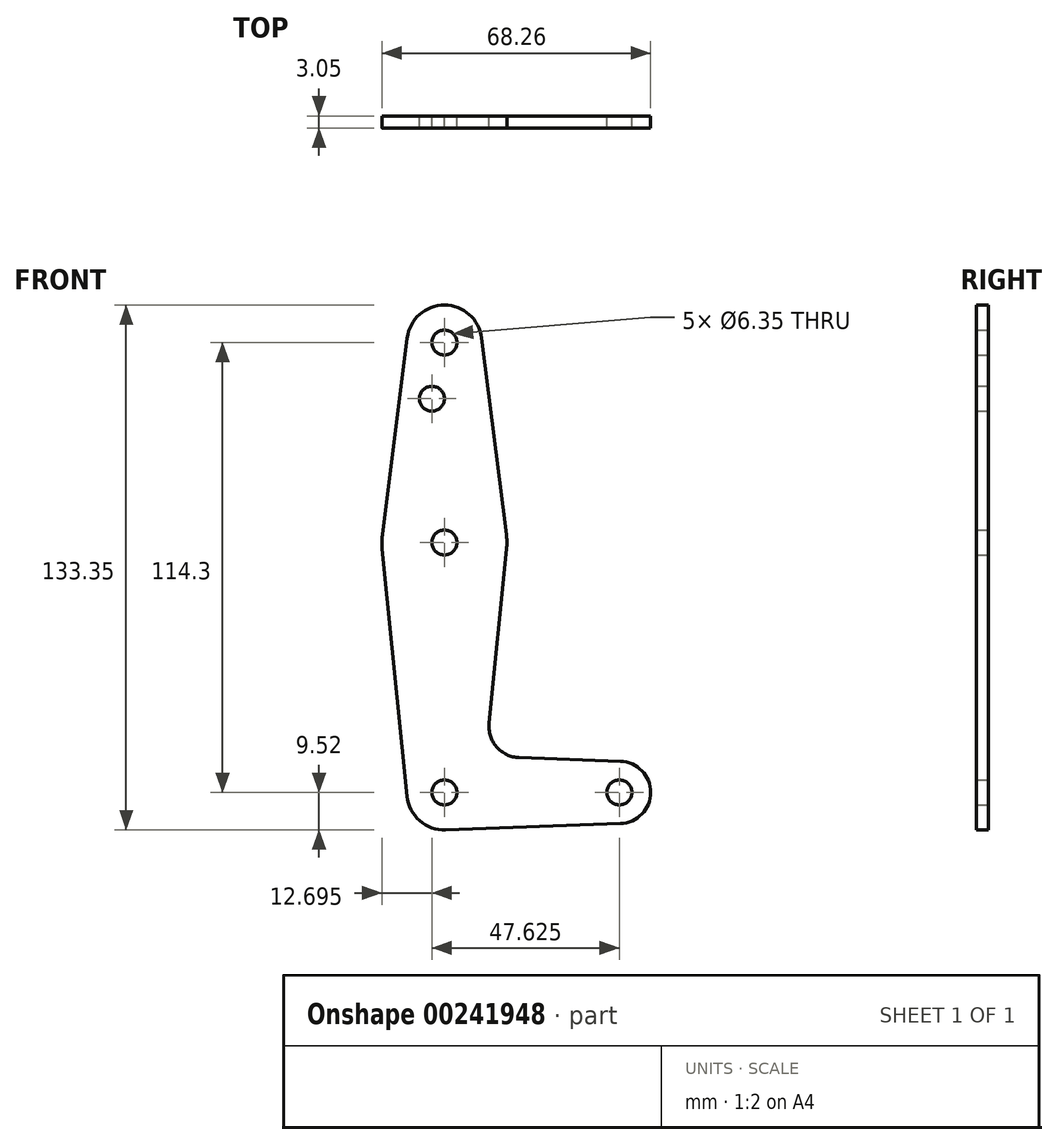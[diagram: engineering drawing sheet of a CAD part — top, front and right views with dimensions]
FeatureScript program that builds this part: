
annotation { "Feature Type Name" : "Feature", "Feature Type Description" : "" }
export const myFeature = defineFeature(function(context is Context, id is Id, definition is map)
    precondition{}
    {
        {
            var Q0;
            Q0=qCreatedBy(makeId("Front.planeOp"),FACE);
            var sketch = newSketch(context, id + "F0", { "sketchPlane" : qUnion([Q0])});
            skLineSegment(sketch, "E0", {"start": v(0, 0) * mm, "end": v(0, 114.3) * mm, "construction": true});
            skLineSegment(sketch, "E1", {"start": v(0, 0) * mm, "end": v(44.45, 0) * mm, "construction": true});
            skCircle(sketch, "E2", {"center": v(0, 114.3) * mm, "radius": 9.53 * mm});
            skCircle(sketch, "E3", {"center": v(0, 63.5) * mm, "radius": 15.88 * mm});
            skCircle(sketch, "E4", {"center": v(0, 0) * mm, "radius": 9.53 * mm});
            skCircle(sketch, "E5", {"center": v(44.45, 0) * mm, "radius": 7.94 * mm});
            skLineSegment(sketch, "E6", {"start": v(-9.45, 115.5) * mm, "end": v(-15.75, 65.48) * mm});
            skLineSegment(sketch, "E7", {"start": v(-9.48, -0.95) * mm, "end": v(-15.8, 61.91) * mm});
            skLineSegment(sketch, "E8", {"start": v(11.34, 17.6) * mm, "end": v(15.8, 61.91) * mm});
            skLineSegment(sketch, "E9", {"start": v(9.45, 115.5) * mm, "end": v(15.75, 65.48) * mm});
            skLineSegment(sketch, "E10", {"start": v(18.97, 8.85) * mm, "end": v(44.73, 7.93) * mm});
            skLineSegment(sketch, "E11", {"start": v(44.73, -7.93) * mm, "end": v(0, -9.53) * mm});
            skCircle(sketch, "E12", {"center": v(0, 114.3) * mm, "radius": 3.18 * mm});
            skCircle(sketch, "E13", {"center": v(0, 63.5) * mm, "radius": 3.18 * mm});
            skCircle(sketch, "E14", {"center": v(0, 0) * mm, "radius": 3.18 * mm});
            skCircle(sketch, "E15", {"center": v(44.45, 0) * mm, "radius": 3.18 * mm});
            skCircle(sketch, "E16", {"center": v(-3.18, 100.03) * mm, "radius": 3.18 * mm});
            skArc(sketch, "E17.filletArc", {"start": v(11.34, 17.6) * mm, "mid": v(13.26, 11.57) * mm, "end": v(18.97, 8.85) * mm});
            skSolve(sketch);
        }
        {
            var Q0;
            Q0=qSketchRegion(id+"F0",true);
            extrude(context, id + "F1", {"entities" : qUnion([Q0]), "depth" : 3.05 * mm});
        }
    });
